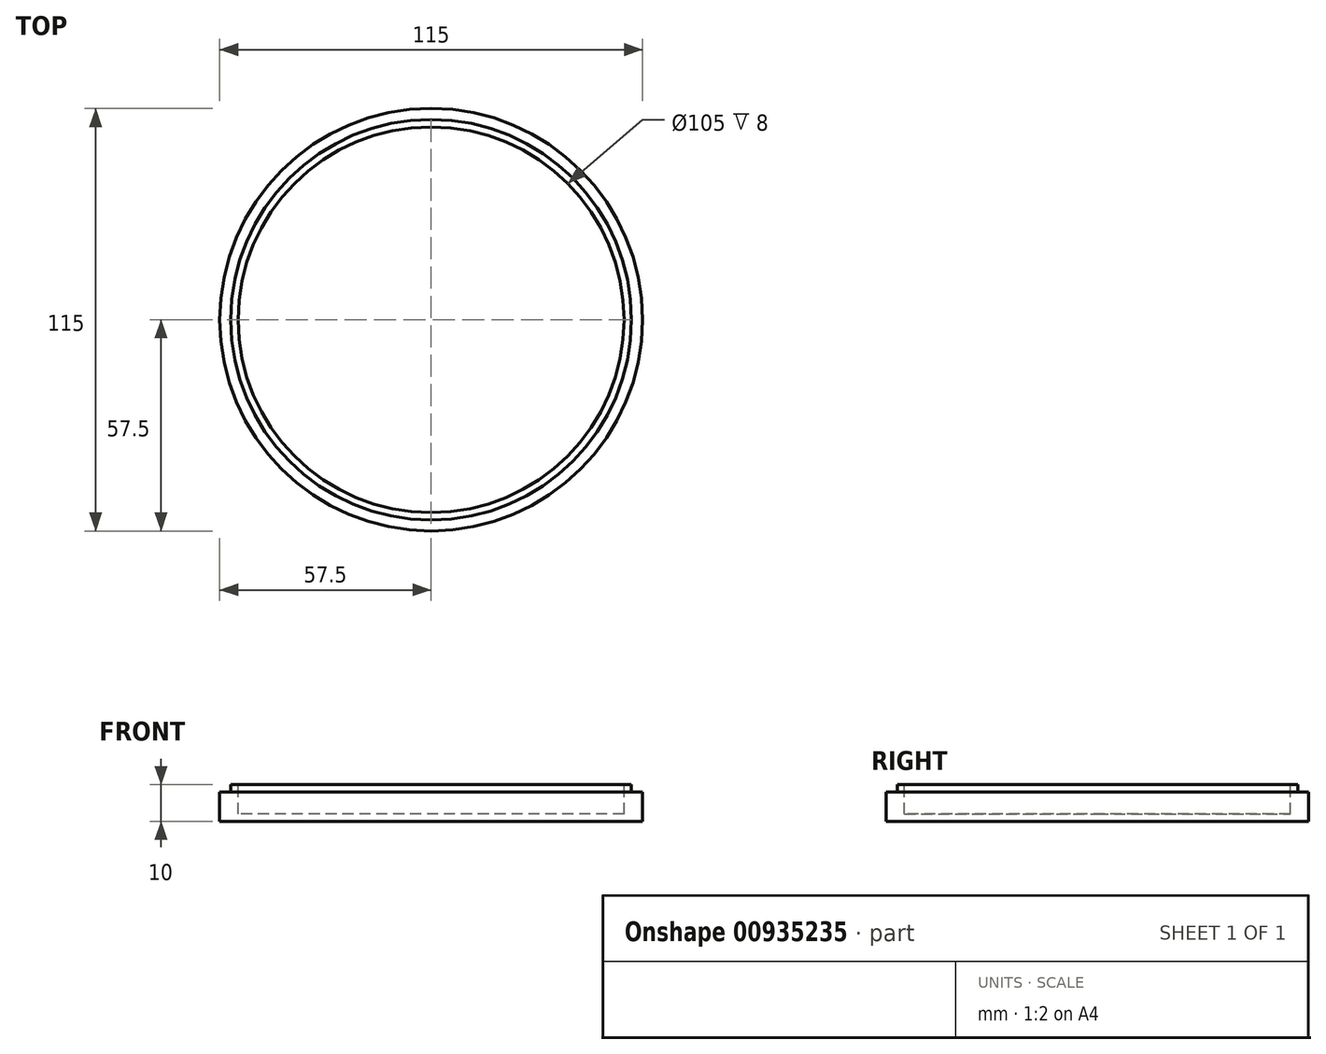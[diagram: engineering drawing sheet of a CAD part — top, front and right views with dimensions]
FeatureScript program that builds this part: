
annotation { "Feature Type Name" : "Feature", "Feature Type Description" : "" }
export const myFeature = defineFeature(function(context is Context, id is Id, definition is map)
    precondition{}
    {
        {
            var Q0;
            Q0=qCreatedBy(makeId("Top.planeOp"),FACE);
            var sketch = newSketch(context, id + "F0", { "sketchPlane" : qUnion([Q0])});
            skCircle(sketch, "E0", {"center": v(0, 0) * mm, "radius": 57.5 * mm});
            skSolve(sketch);
        }
        {
            var Q0;
            Q0=makeQuery(id+"F0.imprint","IMPRINT",FACE,{"disambiguationData":[TD([[makeQuery(id+"F0.imprint","IMPRINT",EDGE,{"derivedFrom":sQuery(id+"F0.wireOp",EDGE,"E0")}),1.0]])]});
            extrude(context, id + "F1", {"entities" : qUnion([Q0]), "depth" : 10 * mm, "offsetDistance" : 25 * mm});
        }
        {
            var Q0;
            Q0=makeQuery(id+"F1.opExtrude","CAP_FACE",FACE,{"disambiguationData":[OSD([sQuery(id+"F0.wireOp",EDGE,"E0")])],"isStart":false});
            var sketch = newSketch(context, id + "F2", { "sketchPlane" : qUnion([Q0])});
            skCircle(sketch, "E1", {"center": v(0, 0) * mm, "radius": 54.5 * mm});
            skSolve(sketch);
        }
        {
            var Q0;
            Q0=makeQuery(id+"F2.imprint","IMPRINT",FACE,{"disambiguationData":[TD([[makeQuery(id+"F2.imprint","IMPRINT",EDGE,{"derivedFrom":sQuery(id+"F2.wireOp",EDGE,"E1")}),-1.0]])]});
            extrude(context, id + "F3", {"entities" : qUnion([Q0]), "operationType" : NewBodyOperationType.REMOVE, "oppositeDirection" : true, "depth" : 2 * mm, "offsetDistance" : 25 * mm});
        }
        {
            var Q0;
            Q0=makeQuery(id+"F1.opExtrude","CAP_FACE",FACE,{"disambiguationData":[OSD([sQuery(id+"F0.wireOp",EDGE,"E0")])],"isStart":false});
            var sketch = newSketch(context, id + "F4", { "sketchPlane" : qUnion([Q0])});
            skCircle(sketch, "E2", {"center": v(0, 0) * mm, "radius": 52.5 * mm});
            skSolve(sketch);
        }
        {
            var Q0;
            Q0=makeQuery(id+"F4.imprint","IMPRINT",FACE,{"disambiguationData":[TD([[makeQuery(id+"F4.imprint","IMPRINT",EDGE,{"derivedFrom":sQuery(id+"F4.wireOp",EDGE,"E2")}),1.0]])]});
            extrude(context, id + "F5", {"entities" : qUnion([Q0]), "operationType" : NewBodyOperationType.REMOVE, "oppositeDirection" : true, "depth" : 8 * mm, "offsetDistance" : 25 * mm});
        }
    });
